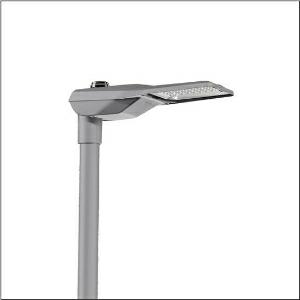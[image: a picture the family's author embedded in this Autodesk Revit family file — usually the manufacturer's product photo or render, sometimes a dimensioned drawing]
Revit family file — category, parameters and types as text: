
# Revit family: streetlight_sl_21_mini___st0_8a_5xe6c37n08jb_d8d6
name_source: partatom
category: Lighting Fixtures
units: mm (PartAtom-declared; Revit-internal decimal feet)

## family parameters
Cut with Voids When Loaded = No
Host = Face
Light Source = No
Part Type = Normal
Room Calculation Point = No
Round Connector Dimension = Use Diameter
Shared = No

## types (1)
- --- (1 x LED, 12830 lm, 87.3 W, 3000K)
    Apparent Load = 87 VA
    CIE Flux Codes = 41 75 97 100 100
    Color Rendering = 70
    Color Temperature = 3000K
    Default Elevation = 1800 mm
    Description = Streetlight SL 21 mini, mast luminaire, primary light control with lens, of PMMA, primary optical cover: cover, of toughened safety glass, transparent, light distribution: ST0.8a, light emission: direct distribution, primary light characteristic: asymmetric, installation type: side-entry, LED, 3G 2.5mm², High Power LED, rated luminous flux: 12.830lm, luminous efficacy: 147lm/W, light colour: 730, colour temperature: 3000K, control gear: NEMA (7pin), control: overheat protection, pre-setting: linear dimming characteristic, constant luminous flux control, time-dependent luminous flux control, flexible luminous flux parameterisation, mains connection: 230..240V, AC, 50/60Hz, connection cable pre-assembled, cable length: 10,5m, wiring characteristics: H05VV-F, start of lifetime: 87W, end of service life: 90W, reduction: 40W, luminaire housing, of diecast aluminium (EN AC-44300), powder-coated, SITECO metallic grey (DB 702S), corrosivity category C5 high according to DIN EN ISO 12944, multi-level sealing system, sealing non-destructively replaceable, inclination adjustable: 0°, 5°, 10°, 15°, length: 628mm, width: 235mm, height: 110mm, spigot size: 42mm (side-entry), mounting height: 4..8m, protection rating (complete): IP66, insulation class (complete): insulation class I (protective earthing), certification: CE, ENEC, ENEC+, VDE, impact resistance: IK10, permissible operating ambient temperature for outdoor applications: -40..+50°C, standard-compliant lighting for roads and squares, packaging unit: 1 piece

Light Distribution: ST0.8a
    Height = 110 mm
    Lamp = 1 x LED
    Lamp Light Flux = 12830 lm
    Lamp Power = 87.3 W
    Lamp count = 1
    Length = 625 mm
    Luminous efficacy = 147 lm/W
    Manufacturer = Siteco
    ModVariant = No
    Model = 5XE6C37N08JB
    Number of Poles = 1
    OnlyDefault = Yes
    Power Factor = 1
    Product Name = Streetlight SL 21 mini | ST0.8a
    Product group = mast luminaire | pylon top
    ProductGroupID = 6100
    Protection Class = Protection class I
    Protection Degree = IP 66
    RLX_Detail_Level = 1
    RLX_Emergency_Light_Flux = 0 lm
    RLX_Emergency_Type = 0
    RLX_Emergency_Type_DB = No
    RlxData = <blob elided: 26069 chars, md5=c3a1aec6>
    Socket = socket
    Standby Power = 0 W
    System Light Flux = 12830 lm
    System Power = 87 W
    Type Comments = factory setting: luminous flux: 100 % | dim-lin: 254 | 915 mA
    Type Image = l_1294379.jpg
    URL = http://relux.com
    VarID = @adj_133447
    Voltage = 0 V
    Weight = 0.00 kg
    Width = 234 mm

## geometry (parser evidence)
native form markers: Blend x4, Sweep x10
no freeform markers — native parametric forms only
